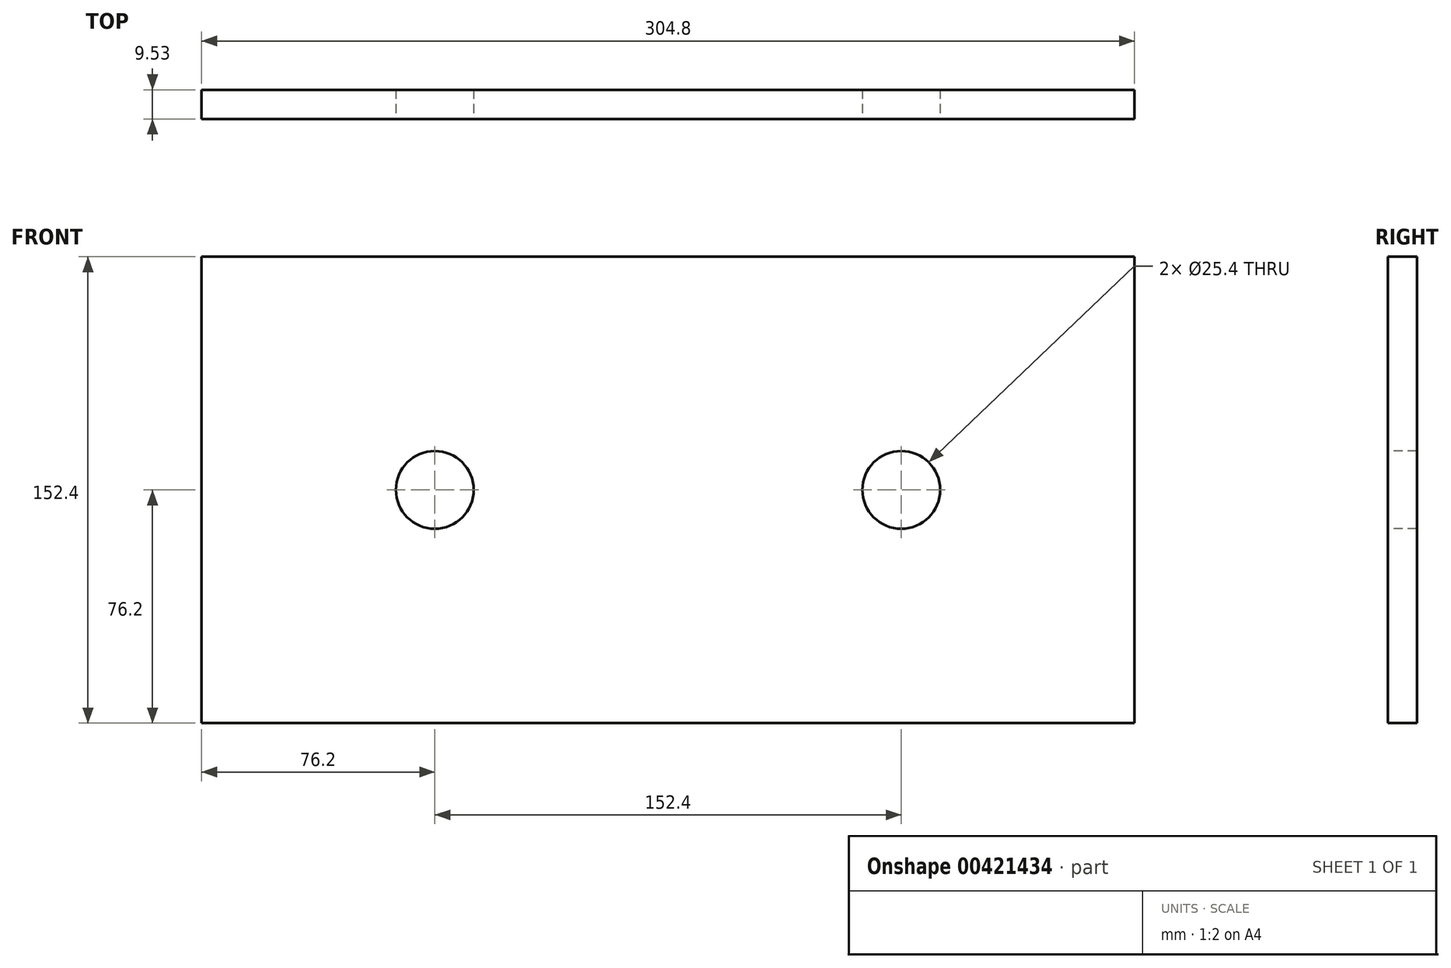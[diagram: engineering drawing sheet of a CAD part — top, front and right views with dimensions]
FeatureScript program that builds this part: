
annotation { "Feature Type Name" : "Feature", "Feature Type Description" : "" }
export const myFeature = defineFeature(function(context is Context, id is Id, definition is map)
    precondition{}
    {
        {
            var Q0;
            Q0=qCreatedBy(makeId("Front.planeOp"),FACE);
            var sketch = newSketch(context, id + "F0", { "sketchPlane" : qUnion([Q0])});
            skLineSegment(sketch, "E0.bottom", {"start": v(0, 0) * mm, "end": v(-304.8, 0) * mm});
            skLineSegment(sketch, "E0.top", {"start": v(0, 152.4) * mm, "end": v(-304.8, 152.4) * mm});
            skLineSegment(sketch, "E0.left", {"start": v(0, 0) * mm, "end": v(0, 152.4) * mm});
            skLineSegment(sketch, "E0.right", {"start": v(-304.8, 0) * mm, "end": v(-304.8, 152.4) * mm});
            skSolve(sketch);
        }
        {
            var Q0;
            Q0=makeQuery(id+"F0.imprint","IMPRINT",FACE,{"disambiguationData":[TD([[makeQuery(id+"F0.imprint","IMPRINT",EDGE,{"derivedFrom":sQuery(id+"F0.wireOp",EDGE,"E0.bottom")}),-1.0]])]});
            extrude(context, id + "F1", {"entities" : qUnion([Q0]), "depth" : 9.52 * mm});
        }
        {
            var Q0;
            Q0=makeQuery(id+"F1.opExtrude","CAP_FACE",FACE,{"disambiguationData":[OSD([sQuery(id+"F0.wireOp",EDGE,"E0.bottom"),sQuery(id+"F0.wireOp",EDGE,"E0.top"),sQuery(id+"F0.wireOp",EDGE,"E0.left"),sQuery(id+"F0.wireOp",EDGE,"E0.right")])],"isStart":false});
            var sketch = newSketch(context, id + "F2", { "sketchPlane" : qUnion([Q0])});
            skCircle(sketch, "E1", {"center": v(-228.6, 76.2) * mm, "radius": 12.7 * mm});
            skCircle(sketch, "E2", {"center": v(-76.2, 76.2) * mm, "radius": 12.7 * mm});
            skLineSegment(sketch, "E3", {"start": v(-228.6, 76.2) * mm, "end": v(-76.2, 76.2) * mm, "construction": true});
            skPoint(sketch, "E4", {"position": v(-152.4, 152.4) * mm});
            skPoint(sketch, "E5", {"position": v(-152.4, 76.2) * mm});
            skPoint(sketch, "E6", {"position": v(-304.8, 76.2) * mm});
            skSolve(sketch);
        }
        {
            var Q0;
            Q0=qSketchRegion(id+"F2",true);
            extrude(context, id + "F3", {"entities" : qUnion([Q0]), "operationType" : NewBodyOperationType.REMOVE, "endBound" : BoundingType.THROUGH_ALL, "oppositeDirection" : true, "depth" : 25.4 * mm});
        }
    });
